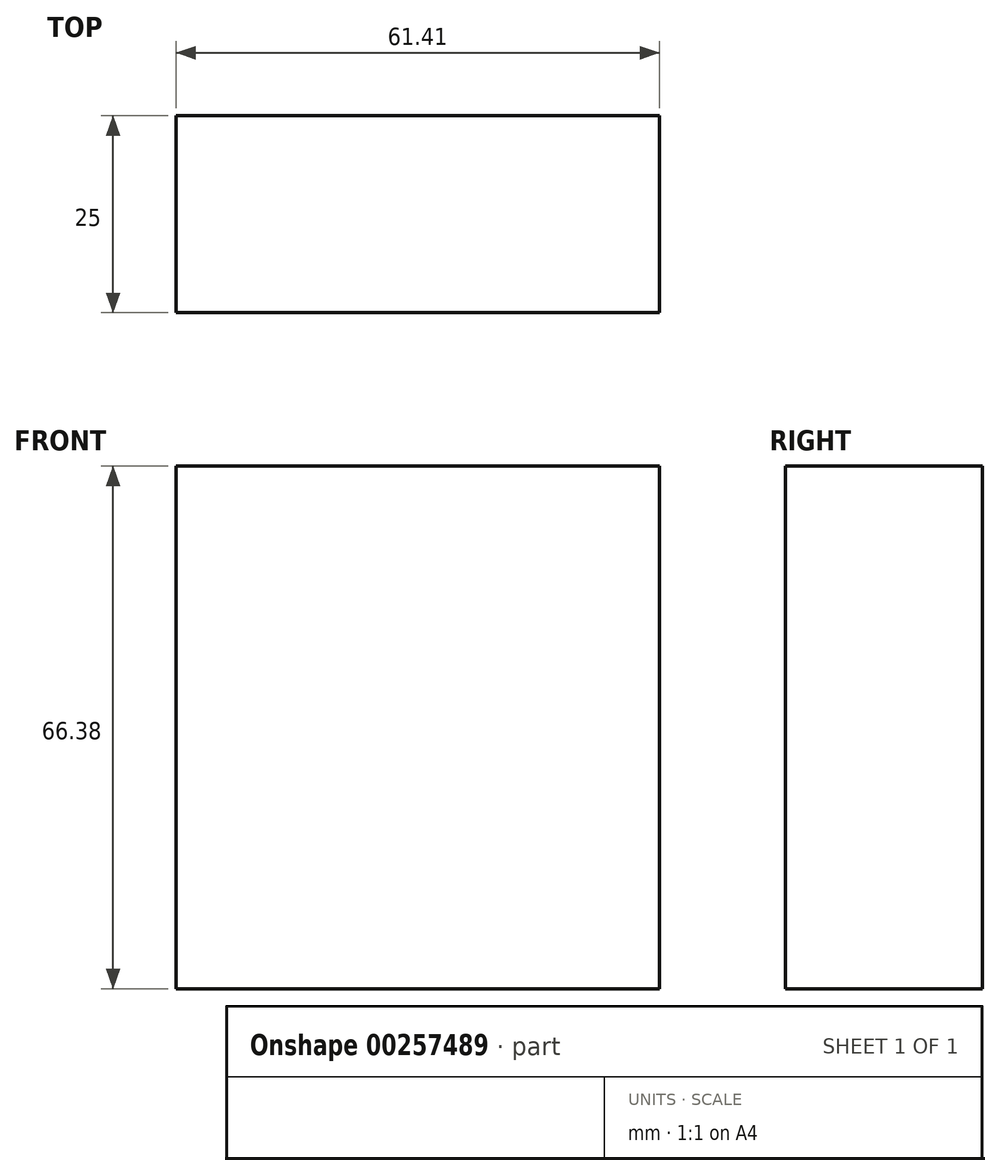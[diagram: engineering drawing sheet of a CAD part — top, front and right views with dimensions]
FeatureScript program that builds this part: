
annotation { "Feature Type Name" : "Feature", "Feature Type Description" : "" }
export const myFeature = defineFeature(function(context is Context, id is Id, definition is map)
    precondition{}
    {
        {
            var Q0;
            Q0=qCreatedBy(makeId("Front.planeOp"),FACE);
            var sketch = newSketch(context, id + "F0", { "sketchPlane" : qUnion([Q0])});
            skLineSegment(sketch, "E0.bottom", {"start": v(-155.54, 71.92) * mm, "end": v(-94.13, 71.92) * mm});
            skLineSegment(sketch, "E0.top", {"start": v(-155.54, 5.54) * mm, "end": v(-94.13, 5.54) * mm});
            skLineSegment(sketch, "E0.left", {"start": v(-155.54, 71.92) * mm, "end": v(-155.54, 5.54) * mm});
            skLineSegment(sketch, "E0.right", {"start": v(-94.13, 71.92) * mm, "end": v(-94.13, 5.54) * mm});
            skSolve(sketch);
        }
        {
            var Q0;
            Q0 = qSketchRegion(id + "F0", true);
            extrude(context, id + "F1", {"entities" : qUnion([Q0]), "depth" : 25 * mm});
        }
    });
